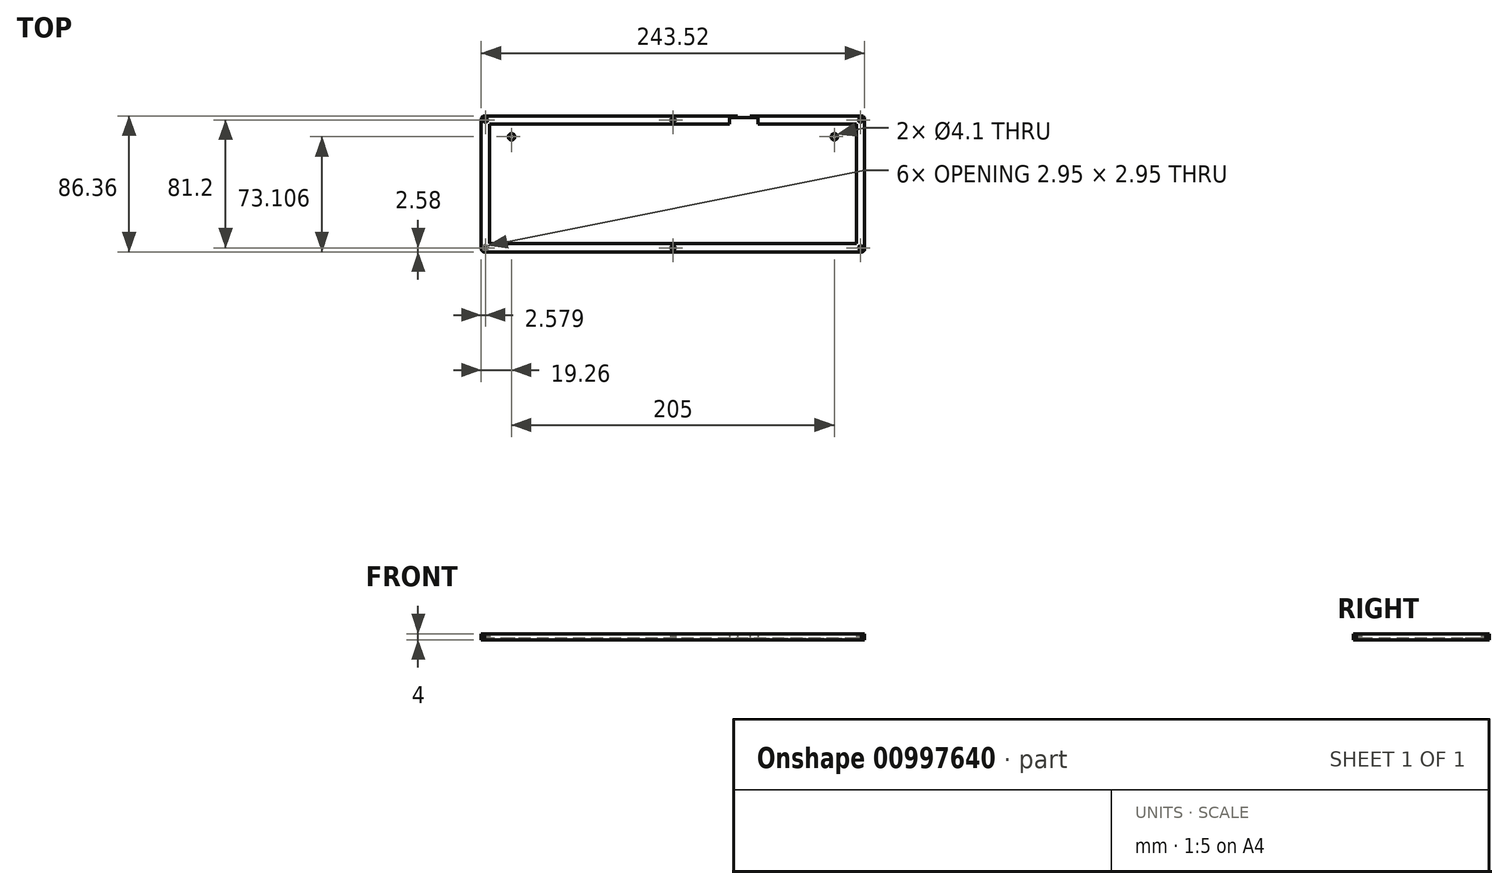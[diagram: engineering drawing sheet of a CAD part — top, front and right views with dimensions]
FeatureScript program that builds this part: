
annotation { "Feature Type Name" : "Feature", "Feature Type Description" : "" }
export const myFeature = defineFeature(function(context is Context, id is Id, definition is map)
    precondition{}
    {
        {
            var Q0;
            Q0=qCreatedBy(makeId("Top.planeOp"),FACE);
            var sketch = newSketch(context, id + "F0", { "sketchPlane" : qUnion([Q0])});
            skLineSegment(sketch, "E0", {"start": v(119.76, 43.17) * mm, "end": v(119.91, 43.17) * mm});
            skLineSegment(sketch, "E1", {"start": v(119.91, 43.17) * mm, "end": v(120.07, 43.15) * mm});
            skLineSegment(sketch, "E2", {"start": v(120.07, 43.15) * mm, "end": v(120.22, 43.12) * mm});
            skLineSegment(sketch, "E3", {"start": v(120.22, 43.12) * mm, "end": v(120.38, 43.08) * mm});
            skLineSegment(sketch, "E4", {"start": v(120.38, 43.08) * mm, "end": v(120.52, 43.02) * mm});
            skLineSegment(sketch, "E5", {"start": v(120.52, 43.02) * mm, "end": v(120.66, 42.96) * mm});
            skLineSegment(sketch, "E6", {"start": v(120.66, 42.96) * mm, "end": v(120.8, 42.88) * mm});
            skLineSegment(sketch, "E7", {"start": v(120.8, 42.88) * mm, "end": v(120.93, 42.8) * mm});
            skLineSegment(sketch, "E8", {"start": v(120.93, 42.8) * mm, "end": v(121.06, 42.7) * mm});
            skLineSegment(sketch, "E9", {"start": v(121.06, 42.7) * mm, "end": v(121.17, 42.6) * mm});
            skLineSegment(sketch, "E10", {"start": v(121.17, 42.6) * mm, "end": v(121.28, 42.47) * mm});
            skLineSegment(sketch, "E11", {"start": v(121.28, 42.47) * mm, "end": v(121.37, 42.35) * mm});
            skLineSegment(sketch, "E12", {"start": v(121.37, 42.35) * mm, "end": v(121.46, 42.22) * mm});
            skLineSegment(sketch, "E13", {"start": v(121.46, 42.22) * mm, "end": v(121.54, 42.08) * mm});
            skLineSegment(sketch, "E14", {"start": v(121.54, 42.08) * mm, "end": v(121.6, 41.94) * mm});
            skLineSegment(sketch, "E15", {"start": v(121.6, 41.94) * mm, "end": v(121.66, 41.8) * mm});
            skLineSegment(sketch, "E16", {"start": v(121.66, 41.8) * mm, "end": v(121.7, 41.64) * mm});
            skLineSegment(sketch, "E17", {"start": v(121.7, 41.64) * mm, "end": v(121.73, 41.49) * mm});
            skLineSegment(sketch, "E18", {"start": v(121.73, 41.49) * mm, "end": v(121.75, 41.33) * mm});
            skLineSegment(sketch, "E19", {"start": v(121.75, 41.33) * mm, "end": v(121.76, 41.18) * mm});
            skLineSegment(sketch, "E20", {"start": v(121.76, 41.18) * mm, "end": v(121.76, -41.18) * mm});
            skLineSegment(sketch, "E21", {"start": v(121.76, -41.18) * mm, "end": v(121.75, -41.33) * mm});
            skLineSegment(sketch, "E22", {"start": v(121.75, -41.33) * mm, "end": v(121.73, -41.49) * mm});
            skLineSegment(sketch, "E23", {"start": v(121.73, -41.49) * mm, "end": v(121.7, -41.64) * mm});
            skLineSegment(sketch, "E24", {"start": v(121.7, -41.64) * mm, "end": v(121.66, -41.8) * mm});
            skLineSegment(sketch, "E25", {"start": v(121.66, -41.8) * mm, "end": v(121.6, -41.94) * mm});
            skLineSegment(sketch, "E26", {"start": v(121.6, -41.94) * mm, "end": v(121.54, -42.08) * mm});
            skLineSegment(sketch, "E27", {"start": v(121.54, -42.08) * mm, "end": v(121.46, -42.22) * mm});
            skLineSegment(sketch, "E28", {"start": v(121.46, -42.22) * mm, "end": v(121.37, -42.35) * mm});
            skLineSegment(sketch, "E29", {"start": v(121.37, -42.35) * mm, "end": v(121.28, -42.47) * mm});
            skLineSegment(sketch, "E30", {"start": v(121.28, -42.47) * mm, "end": v(121.17, -42.6) * mm});
            skLineSegment(sketch, "E31", {"start": v(121.17, -42.6) * mm, "end": v(121.06, -42.7) * mm});
            skLineSegment(sketch, "E32", {"start": v(121.06, -42.7) * mm, "end": v(120.93, -42.8) * mm});
            skLineSegment(sketch, "E33", {"start": v(120.93, -42.8) * mm, "end": v(120.8, -42.88) * mm});
            skLineSegment(sketch, "E34", {"start": v(120.8, -42.88) * mm, "end": v(120.66, -42.96) * mm});
            skLineSegment(sketch, "E35", {"start": v(120.66, -42.96) * mm, "end": v(120.52, -43.02) * mm});
            skLineSegment(sketch, "E36", {"start": v(120.52, -43.02) * mm, "end": v(120.38, -43.08) * mm});
            skLineSegment(sketch, "E37", {"start": v(120.38, -43.08) * mm, "end": v(120.22, -43.12) * mm});
            skLineSegment(sketch, "E38", {"start": v(120.22, -43.12) * mm, "end": v(120.07, -43.15) * mm});
            skLineSegment(sketch, "E39", {"start": v(120.07, -43.15) * mm, "end": v(119.91, -43.17) * mm});
            skLineSegment(sketch, "E40", {"start": v(119.91, -43.17) * mm, "end": v(119.76, -43.17) * mm});
            skLineSegment(sketch, "E41", {"start": v(119.76, -43.17) * mm, "end": v(-119.76, -43.18) * mm});
            skLineSegment(sketch, "E42", {"start": v(-119.76, -43.18) * mm, "end": v(-119.91, -43.17) * mm});
            skLineSegment(sketch, "E43", {"start": v(-119.91, -43.17) * mm, "end": v(-120.07, -43.15) * mm});
            skLineSegment(sketch, "E44", {"start": v(-120.07, -43.15) * mm, "end": v(-120.22, -43.12) * mm});
            skLineSegment(sketch, "E45", {"start": v(-120.22, -43.12) * mm, "end": v(-120.37, -43.08) * mm});
            skLineSegment(sketch, "E46", {"start": v(-120.37, -43.08) * mm, "end": v(-120.52, -43.02) * mm});
            skLineSegment(sketch, "E47", {"start": v(-120.52, -43.02) * mm, "end": v(-120.66, -42.96) * mm});
            skLineSegment(sketch, "E48", {"start": v(-120.66, -42.96) * mm, "end": v(-120.8, -42.88) * mm});
            skLineSegment(sketch, "E49", {"start": v(-120.8, -42.88) * mm, "end": v(-120.93, -42.8) * mm});
            skLineSegment(sketch, "E50", {"start": v(-120.93, -42.8) * mm, "end": v(-121.06, -42.7) * mm});
            skLineSegment(sketch, "E51", {"start": v(-121.06, -42.7) * mm, "end": v(-121.17, -42.6) * mm});
            skLineSegment(sketch, "E52", {"start": v(-121.17, -42.6) * mm, "end": v(-121.28, -42.47) * mm});
            skLineSegment(sketch, "E53", {"start": v(-121.28, -42.47) * mm, "end": v(-121.38, -42.35) * mm});
            skLineSegment(sketch, "E54", {"start": v(-121.38, -42.35) * mm, "end": v(-121.46, -42.22) * mm});
            skLineSegment(sketch, "E55", {"start": v(-121.46, -42.22) * mm, "end": v(-121.54, -42.08) * mm});
            skLineSegment(sketch, "E56", {"start": v(-121.54, -42.08) * mm, "end": v(-121.6, -41.94) * mm});
            skLineSegment(sketch, "E57", {"start": v(-121.6, -41.94) * mm, "end": v(-121.66, -41.8) * mm});
            skLineSegment(sketch, "E58", {"start": v(-121.66, -41.8) * mm, "end": v(-121.7, -41.64) * mm});
            skLineSegment(sketch, "E59", {"start": v(-121.7, -41.64) * mm, "end": v(-121.73, -41.49) * mm});
            skLineSegment(sketch, "E60", {"start": v(-121.73, -41.49) * mm, "end": v(-121.75, -41.33) * mm});
            skLineSegment(sketch, "E61", {"start": v(-121.75, -41.33) * mm, "end": v(-121.76, -41.18) * mm});
            skLineSegment(sketch, "E62", {"start": v(-121.76, -41.18) * mm, "end": v(-121.76, 41.18) * mm});
            skLineSegment(sketch, "E63", {"start": v(-121.76, 41.18) * mm, "end": v(-121.75, 41.33) * mm});
            skLineSegment(sketch, "E64", {"start": v(-121.75, 41.33) * mm, "end": v(-121.73, 41.49) * mm});
            skLineSegment(sketch, "E65", {"start": v(-121.73, 41.49) * mm, "end": v(-121.7, 41.64) * mm});
            skLineSegment(sketch, "E66", {"start": v(-121.7, 41.64) * mm, "end": v(-121.66, 41.8) * mm});
            skLineSegment(sketch, "E67", {"start": v(-121.66, 41.8) * mm, "end": v(-121.6, 41.94) * mm});
            skLineSegment(sketch, "E68", {"start": v(-121.6, 41.94) * mm, "end": v(-121.54, 42.08) * mm});
            skLineSegment(sketch, "E69", {"start": v(-121.54, 42.08) * mm, "end": v(-121.46, 42.22) * mm});
            skLineSegment(sketch, "E70", {"start": v(-121.46, 42.22) * mm, "end": v(-121.38, 42.35) * mm});
            skLineSegment(sketch, "E71", {"start": v(-121.38, 42.35) * mm, "end": v(-121.28, 42.47) * mm});
            skLineSegment(sketch, "E72", {"start": v(-121.28, 42.47) * mm, "end": v(-121.17, 42.6) * mm});
            skLineSegment(sketch, "E73", {"start": v(-121.17, 42.6) * mm, "end": v(-121.06, 42.7) * mm});
            skLineSegment(sketch, "E74", {"start": v(-121.06, 42.7) * mm, "end": v(-120.93, 42.8) * mm});
            skLineSegment(sketch, "E75", {"start": v(-120.93, 42.8) * mm, "end": v(-120.8, 42.88) * mm});
            skLineSegment(sketch, "E76", {"start": v(-120.8, 42.88) * mm, "end": v(-120.66, 42.96) * mm});
            skLineSegment(sketch, "E77", {"start": v(-120.66, 42.96) * mm, "end": v(-120.52, 43.02) * mm});
            skLineSegment(sketch, "E78", {"start": v(-120.52, 43.02) * mm, "end": v(-120.37, 43.08) * mm});
            skLineSegment(sketch, "E79", {"start": v(-120.37, 43.08) * mm, "end": v(-120.22, 43.12) * mm});
            skLineSegment(sketch, "E80", {"start": v(-120.22, 43.12) * mm, "end": v(-120.07, 43.15) * mm});
            skLineSegment(sketch, "E81", {"start": v(-120.07, 43.15) * mm, "end": v(-119.91, 43.17) * mm});
            skLineSegment(sketch, "E82", {"start": v(-119.91, 43.17) * mm, "end": v(-119.76, 43.18) * mm});
            skLineSegment(sketch, "E83", {"start": v(118.73, -39.2) * mm, "end": v(118.32, -39.4) * mm});
            skLineSegment(sketch, "E84", {"start": v(118.32, -39.4) * mm, "end": v(117.99, -39.73) * mm});
            skLineSegment(sketch, "E85", {"start": v(117.99, -39.73) * mm, "end": v(117.78, -40.15) * mm});
            skLineSegment(sketch, "E86", {"start": v(117.78, -40.15) * mm, "end": v(117.7, -40.6) * mm});
            skLineSegment(sketch, "E87", {"start": v(117.7, -40.6) * mm, "end": v(117.78, -41.06) * mm});
            skLineSegment(sketch, "E88", {"start": v(117.78, -41.06) * mm, "end": v(117.99, -41.47) * mm});
            skLineSegment(sketch, "E89", {"start": v(117.99, -41.47) * mm, "end": v(118.32, -41.8) * mm});
            skLineSegment(sketch, "E90", {"start": v(118.32, -41.8) * mm, "end": v(118.73, -42) * mm});
            skLineSegment(sketch, "E91", {"start": v(118.73, -42) * mm, "end": v(119.18, -42.08) * mm});
            skLineSegment(sketch, "E92", {"start": v(119.18, -42.08) * mm, "end": v(119.64, -42) * mm});
            skLineSegment(sketch, "E93", {"start": v(119.64, -42) * mm, "end": v(120.05, -41.8) * mm});
            skLineSegment(sketch, "E94", {"start": v(120.05, -41.8) * mm, "end": v(120.38, -41.47) * mm});
            skLineSegment(sketch, "E95", {"start": v(120.38, -41.47) * mm, "end": v(120.59, -41.06) * mm});
            skLineSegment(sketch, "E96", {"start": v(120.59, -41.06) * mm, "end": v(120.66, -40.6) * mm});
            skLineSegment(sketch, "E97", {"start": v(120.66, -40.6) * mm, "end": v(120.59, -40.15) * mm});
            skLineSegment(sketch, "E98", {"start": v(120.59, -40.15) * mm, "end": v(120.38, -39.73) * mm});
            skLineSegment(sketch, "E99", {"start": v(120.38, -39.73) * mm, "end": v(120.05, -39.4) * mm});
            skLineSegment(sketch, "E100", {"start": v(120.05, -39.4) * mm, "end": v(119.64, -39.2) * mm});
            skLineSegment(sketch, "E101", {"start": v(119.64, -39.2) * mm, "end": v(119.18, -39.13) * mm});
            skLineSegment(sketch, "E102", {"start": v(119.18, -39.13) * mm, "end": v(118.73, -39.2) * mm});
            skLineSegment(sketch, "E103", {"start": v(-0.46, -39.2) * mm, "end": v(-0.87, -39.4) * mm});
            skLineSegment(sketch, "E104", {"start": v(-0.87, -39.4) * mm, "end": v(-1.2, -39.73) * mm});
            skLineSegment(sketch, "E105", {"start": v(-1.2, -39.73) * mm, "end": v(-1.4, -40.15) * mm});
            skLineSegment(sketch, "E106", {"start": v(-1.4, -40.15) * mm, "end": v(-1.47, -40.6) * mm});
            skLineSegment(sketch, "E107", {"start": v(-1.47, -40.6) * mm, "end": v(-1.4, -41.06) * mm});
            skLineSegment(sketch, "E108", {"start": v(-1.4, -41.06) * mm, "end": v(-1.2, -41.47) * mm});
            skLineSegment(sketch, "E109", {"start": v(-1.2, -41.47) * mm, "end": v(-0.87, -41.8) * mm});
            skLineSegment(sketch, "E110", {"start": v(-0.87, -41.8) * mm, "end": v(-0.46, -42) * mm});
            skLineSegment(sketch, "E111", {"start": v(-0.46, -42) * mm, "end": v(0, -42.08) * mm});
            skLineSegment(sketch, "E112", {"start": v(0, -42.08) * mm, "end": v(0.46, -42) * mm});
            skLineSegment(sketch, "E113", {"start": v(0.46, -42) * mm, "end": v(0.87, -41.8) * mm});
            skLineSegment(sketch, "E114", {"start": v(0.87, -41.8) * mm, "end": v(1.2, -41.47) * mm});
            skLineSegment(sketch, "E115", {"start": v(1.2, -41.47) * mm, "end": v(1.4, -41.06) * mm});
            skLineSegment(sketch, "E116", {"start": v(1.4, -41.06) * mm, "end": v(1.48, -40.6) * mm});
            skLineSegment(sketch, "E117", {"start": v(1.48, -40.6) * mm, "end": v(1.4, -40.15) * mm});
            skLineSegment(sketch, "E118", {"start": v(1.4, -40.15) * mm, "end": v(1.2, -39.73) * mm});
            skLineSegment(sketch, "E119", {"start": v(1.2, -39.73) * mm, "end": v(0.87, -39.4) * mm});
            skLineSegment(sketch, "E120", {"start": v(0.87, -39.4) * mm, "end": v(0.46, -39.2) * mm});
            skLineSegment(sketch, "E121", {"start": v(0.46, -39.2) * mm, "end": v(0, -39.13) * mm});
            skLineSegment(sketch, "E122", {"start": v(0, -39.13) * mm, "end": v(-0.46, -39.2) * mm});
            skLineSegment(sketch, "E123", {"start": v(-119.64, -39.2) * mm, "end": v(-120.05, -39.4) * mm});
            skLineSegment(sketch, "E124", {"start": v(-120.05, -39.4) * mm, "end": v(-120.37, -39.73) * mm});
            skLineSegment(sketch, "E125", {"start": v(-120.37, -39.73) * mm, "end": v(-120.58, -40.15) * mm});
            skLineSegment(sketch, "E126", {"start": v(-120.58, -40.15) * mm, "end": v(-120.66, -40.6) * mm});
            skLineSegment(sketch, "E127", {"start": v(-120.66, -40.6) * mm, "end": v(-120.58, -41.06) * mm});
            skLineSegment(sketch, "E128", {"start": v(-120.58, -41.06) * mm, "end": v(-120.37, -41.47) * mm});
            skLineSegment(sketch, "E129", {"start": v(-120.37, -41.47) * mm, "end": v(-120.05, -41.8) * mm});
            skLineSegment(sketch, "E130", {"start": v(-120.05, -41.8) * mm, "end": v(-119.64, -42) * mm});
            skLineSegment(sketch, "E131", {"start": v(-119.64, -42) * mm, "end": v(-119.18, -42.08) * mm});
            skLineSegment(sketch, "E132", {"start": v(-119.18, -42.08) * mm, "end": v(-118.73, -42) * mm});
            skLineSegment(sketch, "E133", {"start": v(-118.73, -42) * mm, "end": v(-118.31, -41.8) * mm});
            skLineSegment(sketch, "E134", {"start": v(-118.31, -41.8) * mm, "end": v(-117.99, -41.47) * mm});
            skLineSegment(sketch, "E135", {"start": v(-117.99, -41.47) * mm, "end": v(-117.78, -41.06) * mm});
            skLineSegment(sketch, "E136", {"start": v(-117.78, -41.06) * mm, "end": v(-117.7, -40.6) * mm});
            skLineSegment(sketch, "E137", {"start": v(-117.7, -40.6) * mm, "end": v(-117.78, -40.15) * mm});
            skLineSegment(sketch, "E138", {"start": v(-117.78, -40.15) * mm, "end": v(-117.99, -39.73) * mm});
            skLineSegment(sketch, "E139", {"start": v(-117.99, -39.73) * mm, "end": v(-118.31, -39.4) * mm});
            skLineSegment(sketch, "E140", {"start": v(-118.31, -39.4) * mm, "end": v(-118.73, -39.2) * mm});
            skLineSegment(sketch, "E141", {"start": v(-118.73, -39.2) * mm, "end": v(-119.18, -39.13) * mm});
            skLineSegment(sketch, "E142", {"start": v(-119.18, -39.13) * mm, "end": v(-119.64, -39.2) * mm});
            skLineSegment(sketch, "E143", {"start": v(116.6, 38.03) * mm, "end": v(116.6, -38.03) * mm});
            skLineSegment(sketch, "E144", {"start": v(116.6, -38.03) * mm, "end": v(-116.6, -38.03) * mm});
            skLineSegment(sketch, "E145", {"start": v(-116.6, -38.03) * mm, "end": v(-116.6, 38.03) * mm});
            skLineSegment(sketch, "E146", {"start": v(-0.46, 42) * mm, "end": v(-0.87, 41.8) * mm});
            skLineSegment(sketch, "E147", {"start": v(-0.87, 41.8) * mm, "end": v(-1.2, 41.47) * mm});
            skLineSegment(sketch, "E148", {"start": v(-1.2, 41.47) * mm, "end": v(-1.4, 41.06) * mm});
            skLineSegment(sketch, "E149", {"start": v(-1.4, 41.06) * mm, "end": v(-1.47, 40.6) * mm});
            skLineSegment(sketch, "E150", {"start": v(-1.47, 40.6) * mm, "end": v(-1.4, 40.15) * mm});
            skLineSegment(sketch, "E151", {"start": v(-1.4, 40.15) * mm, "end": v(-1.2, 39.73) * mm});
            skLineSegment(sketch, "E152", {"start": v(-1.2, 39.73) * mm, "end": v(-0.87, 39.4) * mm});
            skLineSegment(sketch, "E153", {"start": v(-0.87, 39.4) * mm, "end": v(-0.46, 39.2) * mm});
            skLineSegment(sketch, "E154", {"start": v(-0.46, 39.2) * mm, "end": v(0, 39.12) * mm});
            skLineSegment(sketch, "E155", {"start": v(0, 39.12) * mm, "end": v(0.46, 39.2) * mm});
            skLineSegment(sketch, "E156", {"start": v(0.46, 39.2) * mm, "end": v(0.87, 39.4) * mm});
            skLineSegment(sketch, "E157", {"start": v(0.87, 39.4) * mm, "end": v(1.2, 39.73) * mm});
            skLineSegment(sketch, "E158", {"start": v(1.2, 39.73) * mm, "end": v(1.4, 40.15) * mm});
            skLineSegment(sketch, "E159", {"start": v(1.4, 40.15) * mm, "end": v(1.48, 40.6) * mm});
            skLineSegment(sketch, "E160", {"start": v(1.48, 40.6) * mm, "end": v(1.4, 41.06) * mm});
            skLineSegment(sketch, "E161", {"start": v(1.4, 41.06) * mm, "end": v(1.2, 41.47) * mm});
            skLineSegment(sketch, "E162", {"start": v(1.2, 41.47) * mm, "end": v(0.87, 41.8) * mm});
            skLineSegment(sketch, "E163", {"start": v(0.87, 41.8) * mm, "end": v(0.46, 42) * mm});
            skLineSegment(sketch, "E164", {"start": v(0.46, 42) * mm, "end": v(0, 42.07) * mm});
            skLineSegment(sketch, "E165", {"start": v(0, 42.07) * mm, "end": v(-0.46, 42) * mm});
            skLineSegment(sketch, "E166", {"start": v(118.73, 42) * mm, "end": v(118.32, 41.8) * mm});
            skLineSegment(sketch, "E167", {"start": v(118.32, 41.8) * mm, "end": v(117.99, 41.47) * mm});
            skLineSegment(sketch, "E168", {"start": v(117.99, 41.47) * mm, "end": v(117.78, 41.06) * mm});
            skLineSegment(sketch, "E169", {"start": v(117.78, 41.06) * mm, "end": v(117.7, 40.6) * mm});
            skLineSegment(sketch, "E170", {"start": v(117.7, 40.6) * mm, "end": v(117.78, 40.15) * mm});
            skLineSegment(sketch, "E171", {"start": v(117.78, 40.15) * mm, "end": v(117.99, 39.73) * mm});
            skLineSegment(sketch, "E172", {"start": v(117.99, 39.73) * mm, "end": v(118.32, 39.4) * mm});
            skLineSegment(sketch, "E173", {"start": v(118.32, 39.4) * mm, "end": v(118.73, 39.2) * mm});
            skLineSegment(sketch, "E174", {"start": v(118.73, 39.2) * mm, "end": v(119.18, 39.12) * mm});
            skLineSegment(sketch, "E175", {"start": v(119.18, 39.12) * mm, "end": v(119.64, 39.2) * mm});
            skLineSegment(sketch, "E176", {"start": v(119.64, 39.2) * mm, "end": v(120.05, 39.4) * mm});
            skLineSegment(sketch, "E177", {"start": v(120.05, 39.4) * mm, "end": v(120.38, 39.73) * mm});
            skLineSegment(sketch, "E178", {"start": v(120.38, 39.73) * mm, "end": v(120.59, 40.15) * mm});
            skLineSegment(sketch, "E179", {"start": v(120.59, 40.15) * mm, "end": v(120.66, 40.6) * mm});
            skLineSegment(sketch, "E180", {"start": v(120.66, 40.6) * mm, "end": v(120.59, 41.06) * mm});
            skLineSegment(sketch, "E181", {"start": v(120.59, 41.06) * mm, "end": v(120.38, 41.47) * mm});
            skLineSegment(sketch, "E182", {"start": v(120.38, 41.47) * mm, "end": v(120.05, 41.8) * mm});
            skLineSegment(sketch, "E183", {"start": v(120.05, 41.8) * mm, "end": v(119.64, 42) * mm});
            skLineSegment(sketch, "E184", {"start": v(119.64, 42) * mm, "end": v(119.18, 42.07) * mm});
            skLineSegment(sketch, "E185", {"start": v(119.18, 42.07) * mm, "end": v(118.73, 42) * mm});
            skLineSegment(sketch, "E186", {"start": v(-119.64, 42) * mm, "end": v(-120.05, 41.8) * mm});
            skLineSegment(sketch, "E187", {"start": v(-120.05, 41.8) * mm, "end": v(-120.37, 41.47) * mm});
            skLineSegment(sketch, "E188", {"start": v(-120.37, 41.47) * mm, "end": v(-120.58, 41.06) * mm});
            skLineSegment(sketch, "E189", {"start": v(-120.58, 41.06) * mm, "end": v(-120.66, 40.6) * mm});
            skLineSegment(sketch, "E190", {"start": v(-120.66, 40.6) * mm, "end": v(-120.58, 40.15) * mm});
            skLineSegment(sketch, "E191", {"start": v(-120.58, 40.15) * mm, "end": v(-120.37, 39.73) * mm});
            skLineSegment(sketch, "E192", {"start": v(-120.37, 39.73) * mm, "end": v(-120.05, 39.4) * mm});
            skLineSegment(sketch, "E193", {"start": v(-120.05, 39.4) * mm, "end": v(-119.64, 39.2) * mm});
            skLineSegment(sketch, "E194", {"start": v(-119.64, 39.2) * mm, "end": v(-119.18, 39.12) * mm});
            skLineSegment(sketch, "E195", {"start": v(-119.18, 39.12) * mm, "end": v(-118.73, 39.2) * mm});
            skLineSegment(sketch, "E196", {"start": v(-118.73, 39.2) * mm, "end": v(-118.31, 39.4) * mm});
            skLineSegment(sketch, "E197", {"start": v(-118.31, 39.4) * mm, "end": v(-117.99, 39.73) * mm});
            skLineSegment(sketch, "E198", {"start": v(-117.99, 39.73) * mm, "end": v(-117.78, 40.15) * mm});
            skLineSegment(sketch, "E199", {"start": v(-117.78, 40.15) * mm, "end": v(-117.7, 40.6) * mm});
            skLineSegment(sketch, "E200", {"start": v(-117.7, 40.6) * mm, "end": v(-117.78, 41.06) * mm});
            skLineSegment(sketch, "E201", {"start": v(-117.78, 41.06) * mm, "end": v(-117.99, 41.47) * mm});
            skLineSegment(sketch, "E202", {"start": v(-117.99, 41.47) * mm, "end": v(-118.31, 41.8) * mm});
            skLineSegment(sketch, "E203", {"start": v(-118.31, 41.8) * mm, "end": v(-118.73, 42) * mm});
            skLineSegment(sketch, "E204", {"start": v(-118.73, 42) * mm, "end": v(-119.18, 42.07) * mm});
            skLineSegment(sketch, "E205", {"start": v(-119.18, 42.07) * mm, "end": v(-119.64, 42) * mm});
            skLineSegment(sketch, "E206", {"start": v(36.05, 42.16) * mm, "end": v(36.05, 38.03) * mm});
            skLineSegment(sketch, "E207", {"start": v(53.95, 42.16) * mm, "end": v(53.95, 38.03) * mm});
            skLineSegment(sketch, "E208", {"start": v(53.95, 38.03) * mm, "end": v(116.6, 38.03) * mm});
            skLineSegment(sketch, "E209", {"start": v(36.05, 38.03) * mm, "end": v(-116.6, 38.03) * mm});
            skLineSegment(sketch, "E210", {"start": v(49, 42.16) * mm, "end": v(49, 43.18) * mm});
            skLineSegment(sketch, "E211", {"start": v(41, 42.16) * mm, "end": v(41, 43.18) * mm});
            skLineSegment(sketch, "E212", {"start": v(41, 42.16) * mm, "end": v(36.05, 42.16) * mm});
            skLineSegment(sketch, "E213", {"start": v(49, 42.16) * mm, "end": v(53.95, 42.16) * mm});
            skLineSegment(sketch, "E214", {"start": v(49, 43.18) * mm, "end": v(119.76, 43.17) * mm});
            skLineSegment(sketch, "E215", {"start": v(41, 43.18) * mm, "end": v(-119.76, 43.18) * mm});
            skLineSegment(sketch, "E216", {"start": v(41, 42.16) * mm, "end": v(49, 42.16) * mm});
            skLineSegment(sketch, "E217", {"start": v(41, 43.18) * mm, "end": v(49, 43.18) * mm});
            skSolve(sketch);
        }
        {
            var Q0;
            Q0=makeQuery(id+"F0.imprint","IMPRINT",FACE,{"disambiguationData":[TD([[makeQuery(id+"F0.imprint","IMPRINT",EDGE,{"derivedFrom":sQuery(id+"F0.wireOp",EDGE,"E143")}),-1.0]])]});
            extrude(context, id + "F1", {"entities" : qUnion([Q0]), "depth" : 1 * mm, "offsetDistance" : 25 * mm});
        }
        {
            var Q0;
            Q0=makeQuery(id+"F0.imprint","IMPRINT",FACE,{"disambiguationData":[TD([[makeQuery(id+"F0.imprint","IMPRINT",EDGE,{"derivedFrom":sQuery(id+"F0.wireOp",EDGE,"E0")}),-1.0]])]});
            extrude(context, id + "F2", {"entities" : qUnion([Q0]), "operationType" : NewBodyOperationType.ADD, "depth" : 4 * mm, "offsetDistance" : 25 * mm});
        }
        {
            var Q0;
            Q0=makeQuery(id+"F1.opExtrude","CAP_FACE",FACE,{"disambiguationData":[OSD([sQuery(id+"F0.wireOp",EDGE,"E143"),sQuery(id+"F0.wireOp",EDGE,"E144"),sQuery(id+"F0.wireOp",EDGE,"E145"),sQuery(id+"F0.wireOp",EDGE,"E206"),sQuery(id+"F0.wireOp",EDGE,"E207"),sQuery(id+"F0.wireOp",EDGE,"E208"),sQuery(id+"F0.wireOp",EDGE,"E209"),sQuery(id+"F0.wireOp",EDGE,"E212"),sQuery(id+"F0.wireOp",EDGE,"E213"),sQuery(id+"F0.wireOp",EDGE,"E216")])],"isStart":false});
            var sketch = newSketch(context, id + "F3", { "sketchPlane" : qUnion([Q0])});
            skLineSegment(sketch, "E218", {"start": v(0, 38.03) * mm, "end": v(0, 29.93) * mm});
            skLineSegment(sketch, "E219", {"start": v(0, 29.93) * mm, "end": v(102.5, 29.93) * mm});
            skLineSegment(sketch, "E220", {"start": v(0, 29.93) * mm, "end": v(-102.5, 29.93) * mm});
            skCircle(sketch, "E221", {"center": v(-102.5, 29.93) * mm, "radius": 2.05 * mm});
            skCircle(sketch, "E222", {"center": v(102.5, 29.93) * mm, "radius": 2.05 * mm});
            skSolve(sketch);
        }
        {
            var Q0;
            Q0=makeQuery(id+"F3.imprint","IMPRINT",FACE,{"disambiguationData":[TD([[makeQuery(id+"F3.imprint","IMPRINT",EDGE,{"derivedFrom":sQuery(id+"F3.wireOp",EDGE,"E221")}),1.0]])]});
            var Q1;
            Q1=makeQuery(id+"F3.imprint","IMPRINT",FACE,{"disambiguationData":[TD([[makeQuery(id+"F3.imprint","IMPRINT",EDGE,{"derivedFrom":sQuery(id+"F3.wireOp",EDGE,"E222")}),1.0]])]});
            extrude(context, id + "F4", {"entities" : qUnion([Q0, Q1]), "operationType" : NewBodyOperationType.REMOVE, "oppositeDirection" : true, "depth" : 25 * mm, "offsetDistance" : 25 * mm});
        }
    });
